# Revit family: Building-SurfaceMountingEnclosures-GEWISS-40CDK-ENCLOSURES_IP65_3X
name_source: partatom
category: Apparecchi elettrici
revit_build: Autodesk Revit 2016 (Build: 20161004_0715(x64)
units: mm (PartAtom-declared; Revit-internal decimal feet)

## family parameters
Condiviso = No
Host = Superficie
Mantenere orientamento annotazione = Sì
Numero OmniClass = 23.80.30.11.17
Punto di calcolo locali = Sì
Quota connettore circolare = Usa diametro
Taglio con vuoti quando caricato = No
Tipo di parte = Normale
Titolo OmniClass = Distribution Boards and Control Panels

## types (2) — shared parameters
Accessories for insulation restoring = Screwcaps (GW44623) or fixing brackets in resin (GW44621)
Catalogue = BUILDING
Catalogue Range = 40 CDK
Colour = Grey RAL 7035
Diametro_tubazione = 30 mm  [stored 0.0984252 ft]
Dimensione_modulo = 18 mm
Door colour = Smoked Transparent
Electrocod = 0321
Glow Wire Test = 650°C
H_finestratura = 45 mm  [stored 0.147638 ft]
H_quadro = 655 mm  [stored 2.14895 ft]
IDF = 776dcc74-c8dd-4db0-98ea-e49dd677a339
IDT = 68f9e14e-b0aa-41f9-8f3c-b00676268cd7
IP degree = IP65
Insulation class = II (according to IEC 61140 standards)
Insulation voltage: = 1000 V according to EN 62208 both in ac as well as in dc
L_finestratura = 324 mm  [stored 1.06299 ft]
L_quadro = 410 mm  [stored 1.34514 ft]
N.M. = 18
Operating temperature = -25 +60 °C
Produttore = GEWISS S.p.A.
Prondita_quadro = 140 mm  [stored 0.459318 ft]
Prospetto di default = 1219 mm
QUADRO = FINITURA BIANCA
Rated current: = 125A
Rated insulation voltage (Ui) = 1000 V
Rated voltage = 400V
SEO = Board
Shock resistance = IK09
Spostamento_x_ET = 1000 mm  [stored 3.28084 ft]
Standard = EN 60670-1 (CEI 23-48) IEC60670-24 CEI 23-49
Standard. = EN 60670-1 (CEI 23-48) IEC60670-24 CEI 23-49
Technical sheet = https://www.gewiss.com
Thermo-pressure with ball = 70
Type of material = Halogen-free in compliance with EN 60754-2
URL = https://www.gewiss.com
Version file RFA = 18.0
fase1 = 0 VA
voltaggio_quadro = 0 V

## per-type parameters (varying)
| type | Descrizione | Dispersible power (W) | EAN code | Max. installable terminal blocks | Modello | No. of modules EN 50022 | No. of modules EN 50022: | Outer dim. LxHxD (mm) |
| GW40108 - SUR. MOU. DISTRIB.BOARD 54M.(18X3) IP65 | SUR. MOU. DISTRIB.BOARD 54M.(18X3) IP65 | 66 | 8011564062252 | 2 x18 modules | GW40108 | 54 (18x3) | 54 (18x3) | 410x655x140 |
| GW40105 - SUR. MOU. DISTRIB.BOARD 36M.(12X3) IP65 | SUR. MOU. DISTRIB.BOARD 36M.(12X3) IP65 | 42 | 8011564111370 | 3 x 12 modules | GW40105 | 36 (12x3) | 36 (12x3) | 298x570x140 |

note: source unit labels omitted for Thermo-pressure with ball — the stored unit's dimension contradicts the parameter name (converter mislabeling)

note: [stored X ft] marks values corroborated as IEEE doubles in the binary element streams (Revit-internal decimal feet)

## geometry (parser evidence)
native form markers: Sweep x1
no freeform markers — native parametric forms only
